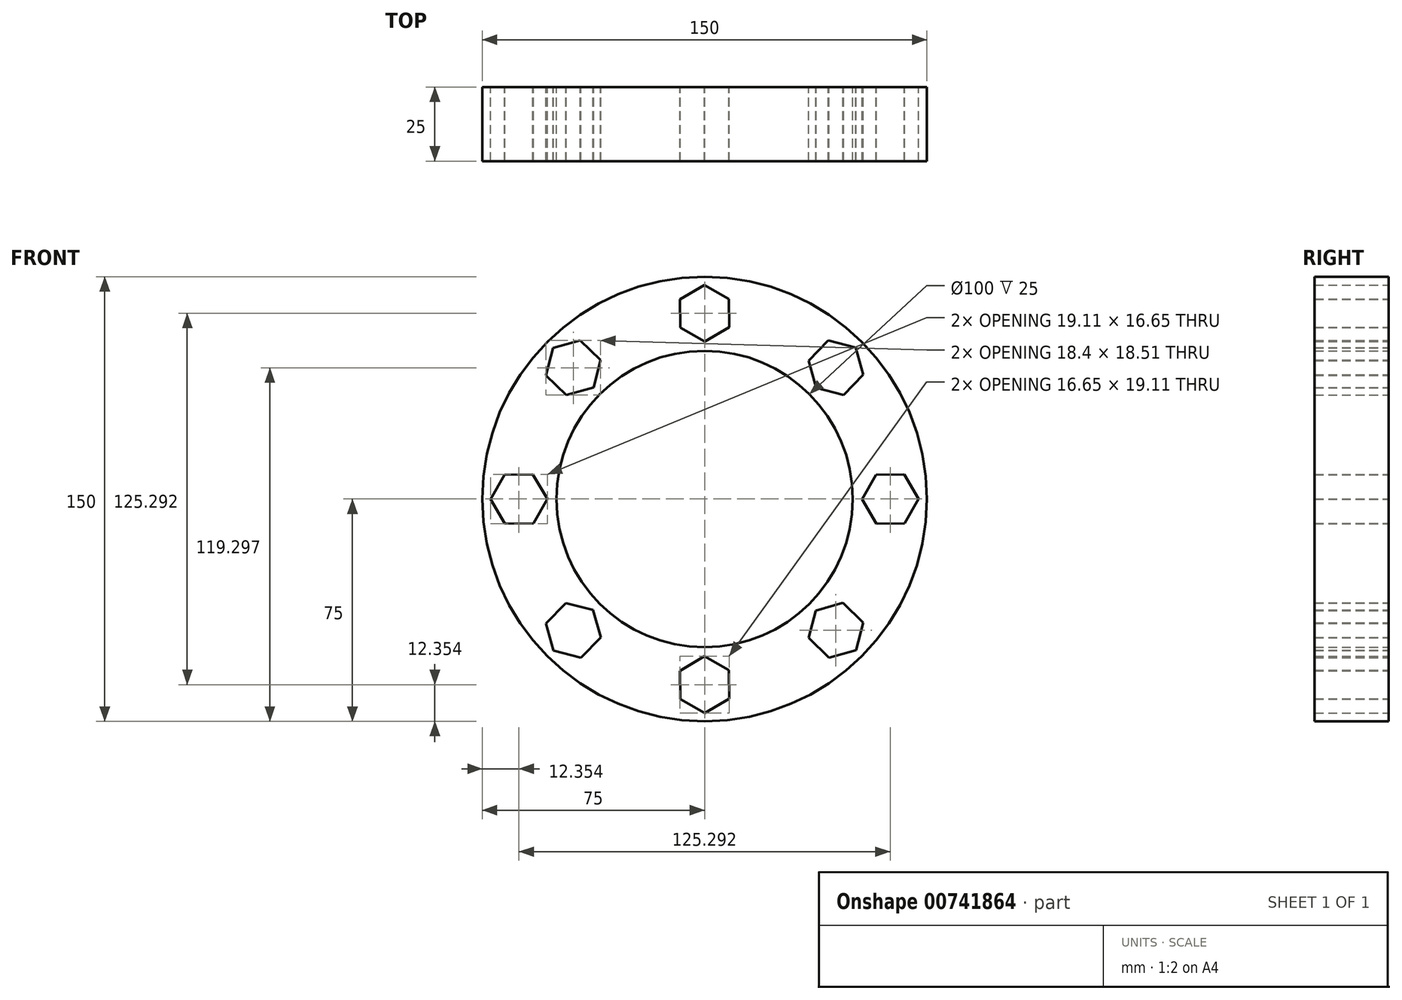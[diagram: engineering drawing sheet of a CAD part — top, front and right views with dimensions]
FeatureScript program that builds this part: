
annotation { "Feature Type Name" : "Feature", "Feature Type Description" : "" }
export const myFeature = defineFeature(function(context is Context, id is Id, definition is map)
    precondition{}
    {
        {
            var Q0;
            Q0=qCreatedBy(makeId("Front.planeOp"),FACE);
            var sketch = newSketch(context, id + "F0", { "sketchPlane" : qUnion([Q0])});
            skCircle(sketch, "E0", {"center": v(0, 0) * mm, "radius": 75 * mm});
            skCircle(sketch, "E1", {"center": v(0, 0) * mm, "radius": 50 * mm});
            skCircle(sketch, "E2.cCircle", {"center": v(0, 62.65) * mm, "radius": 8.27 * mm, "construction": true});
            skLineSegment(sketch, "E2.0", {"start": v(-0.1, 72.2) * mm, "end": v(8.22, 67.52) * mm});
            skLineSegment(sketch, "E2.1", {"start": v(8.22, 67.52) * mm, "end": v(8.33, 57.96) * mm});
            skLineSegment(sketch, "E2.2", {"start": v(8.33, 57.96) * mm, "end": v(0.1, 53.1) * mm});
            skLineSegment(sketch, "E2.3", {"start": v(0.1, 53.1) * mm, "end": v(-8.22, 57.78) * mm});
            skLineSegment(sketch, "E2.4", {"start": v(-8.22, 57.78) * mm, "end": v(-8.33, 67.33) * mm});
            skLineSegment(sketch, "E2.5", {"start": v(-8.33, 67.33) * mm, "end": v(-0.1, 72.2) * mm});
            skPoint(sketch, "E2.0.midPoint", {"position": v(4.06, 69.86) * mm});
            skLineSegment(sketch, "E3.1.0", {"start": v(-51.13, 50.98) * mm, "end": v(-41.93, 53.55) * mm});
            skLineSegment(sketch, "E3.1.1", {"start": v(-41.93, 53.55) * mm, "end": v(-35.1, 46.87) * mm});
            skLineSegment(sketch, "E3.1.2", {"start": v(-35.1, 46.87) * mm, "end": v(-37.47, 37.62) * mm});
            skLineSegment(sketch, "E3.1.3", {"start": v(-37.47, 37.62) * mm, "end": v(-46.67, 35.04) * mm});
            skLineSegment(sketch, "E3.1.4", {"start": v(-46.67, 35.04) * mm, "end": v(-53.5, 41.72) * mm});
            skLineSegment(sketch, "E3.1.5", {"start": v(-53.5, 41.72) * mm, "end": v(-51.13, 50.98) * mm});
            skCircle(sketch, "E3.1.6", {"center": v(-44.3, 44.3) * mm, "radius": 8.27 * mm, "construction": true});
            skLineSegment(sketch, "E3.2.0", {"start": v(-72.2, -0.1) * mm, "end": v(-67.52, 8.22) * mm});
            skLineSegment(sketch, "E3.2.1", {"start": v(-67.52, 8.22) * mm, "end": v(-57.96, 8.33) * mm});
            skLineSegment(sketch, "E3.2.2", {"start": v(-57.96, 8.33) * mm, "end": v(-53.1, 0.1) * mm});
            skLineSegment(sketch, "E3.2.3", {"start": v(-53.1, 0.1) * mm, "end": v(-57.78, -8.22) * mm});
            skLineSegment(sketch, "E3.2.4", {"start": v(-57.78, -8.22) * mm, "end": v(-67.33, -8.33) * mm});
            skLineSegment(sketch, "E3.2.5", {"start": v(-67.33, -8.33) * mm, "end": v(-72.2, -0.1) * mm});
            skCircle(sketch, "E3.2.6", {"center": v(-62.65, 0) * mm, "radius": 8.27 * mm, "construction": true});
            skLineSegment(sketch, "E3.3.0", {"start": v(-50.98, -51.13) * mm, "end": v(-53.55, -41.93) * mm});
            skLineSegment(sketch, "E3.3.1", {"start": v(-53.55, -41.93) * mm, "end": v(-46.87, -35.1) * mm});
            skLineSegment(sketch, "E3.3.2", {"start": v(-46.87, -35.1) * mm, "end": v(-37.62, -37.47) * mm});
            skLineSegment(sketch, "E3.3.3", {"start": v(-37.62, -37.47) * mm, "end": v(-35.04, -46.67) * mm});
            skLineSegment(sketch, "E3.3.4", {"start": v(-35.04, -46.67) * mm, "end": v(-41.72, -53.5) * mm});
            skLineSegment(sketch, "E3.3.5", {"start": v(-41.72, -53.5) * mm, "end": v(-50.98, -51.13) * mm});
            skCircle(sketch, "E3.3.6", {"center": v(-44.3, -44.3) * mm, "radius": 8.27 * mm, "construction": true});
            skLineSegment(sketch, "E3.4.0", {"start": v(0.1, -72.2) * mm, "end": v(-8.22, -67.52) * mm});
            skLineSegment(sketch, "E3.4.1", {"start": v(-8.22, -67.52) * mm, "end": v(-8.33, -57.96) * mm});
            skLineSegment(sketch, "E3.4.2", {"start": v(-8.33, -57.96) * mm, "end": v(-0.1, -53.1) * mm});
            skLineSegment(sketch, "E3.4.3", {"start": v(-0.1, -53.1) * mm, "end": v(8.22, -57.78) * mm});
            skLineSegment(sketch, "E3.4.4", {"start": v(8.22, -57.78) * mm, "end": v(8.33, -67.33) * mm});
            skLineSegment(sketch, "E3.4.5", {"start": v(8.33, -67.33) * mm, "end": v(0.1, -72.2) * mm});
            skCircle(sketch, "E3.4.6", {"center": v(0, -62.65) * mm, "radius": 8.27 * mm, "construction": true});
            skLineSegment(sketch, "E3.5.0", {"start": v(51.13, -50.98) * mm, "end": v(41.93, -53.55) * mm});
            skLineSegment(sketch, "E3.5.1", {"start": v(41.93, -53.55) * mm, "end": v(35.1, -46.87) * mm});
            skLineSegment(sketch, "E3.5.2", {"start": v(35.1, -46.87) * mm, "end": v(37.47, -37.62) * mm});
            skLineSegment(sketch, "E3.5.3", {"start": v(37.47, -37.62) * mm, "end": v(46.67, -35.04) * mm});
            skLineSegment(sketch, "E3.5.4", {"start": v(46.67, -35.04) * mm, "end": v(53.5, -41.72) * mm});
            skLineSegment(sketch, "E3.5.5", {"start": v(53.5, -41.72) * mm, "end": v(51.13, -50.98) * mm});
            skCircle(sketch, "E3.5.6", {"center": v(44.3, -44.3) * mm, "radius": 8.27 * mm, "construction": true});
            skLineSegment(sketch, "E3.6.0", {"start": v(72.2, 0.1) * mm, "end": v(67.52, -8.22) * mm});
            skLineSegment(sketch, "E3.6.1", {"start": v(67.52, -8.22) * mm, "end": v(57.96, -8.33) * mm});
            skLineSegment(sketch, "E3.6.2", {"start": v(57.96, -8.33) * mm, "end": v(53.1, -0.1) * mm});
            skLineSegment(sketch, "E3.6.3", {"start": v(53.1, -0.1) * mm, "end": v(57.78, 8.22) * mm});
            skLineSegment(sketch, "E3.6.4", {"start": v(57.78, 8.22) * mm, "end": v(67.33, 8.33) * mm});
            skLineSegment(sketch, "E3.6.5", {"start": v(67.33, 8.33) * mm, "end": v(72.2, 0.1) * mm});
            skCircle(sketch, "E3.6.6", {"center": v(62.65, 0) * mm, "radius": 8.27 * mm, "construction": true});
            skLineSegment(sketch, "E3.7.0", {"start": v(50.98, 51.13) * mm, "end": v(53.55, 41.93) * mm});
            skLineSegment(sketch, "E3.7.1", {"start": v(53.55, 41.93) * mm, "end": v(46.87, 35.1) * mm});
            skLineSegment(sketch, "E3.7.2", {"start": v(46.87, 35.1) * mm, "end": v(37.62, 37.47) * mm});
            skLineSegment(sketch, "E3.7.3", {"start": v(37.62, 37.47) * mm, "end": v(35.04, 46.67) * mm});
            skLineSegment(sketch, "E3.7.4", {"start": v(35.04, 46.67) * mm, "end": v(41.72, 53.5) * mm});
            skLineSegment(sketch, "E3.7.5", {"start": v(41.72, 53.5) * mm, "end": v(50.98, 51.13) * mm});
            skCircle(sketch, "E3.7.6", {"center": v(44.3, 44.3) * mm, "radius": 8.27 * mm, "construction": true});
            skSolve(sketch);
        }
        {
            var Q0;
            Q0 = qSketchRegion(id + "F0", true);
            extrude(context, id + "F1", {"entities" : qUnion([Q0]), "depth" : 25 * mm, "offsetDistance" : 25 * mm});
        }
    });
